# Revit family: Rheem AmbiPower 280e
name_source: partatom
category: Plumbing Fixtures
units: mm (PartAtom-declared; Revit-internal decimal feet)

## family parameters
Always vertical = Yes
Cut with Voids When Loaded = No
Enable Cutting in Views = No
Maintain Annotation Orientation = No
OmniClass Number = 23.45.00.00
OmniClass Title = Sanitary, Laundry, and Cleaning Equipment
Part Type = Normal
Room Calculation Point = No
Round Connector Dimension = Use Diameter
Shared = No
Work Plane-Based = No

## types (1)
- Rheem AmbiPower 280e
    Boost Capacity = 280.0 L
    Coefficient of Performance @19°C = 5.2
    Default Elevation = 0 mm  [stored 0 ft]
    Description = AmbiPower 280e Heat Pump Water Heater
    Electric heating unit rating @ 240 V = 2400 W
    Heater weight - cartoned = 135.00 kg
    Heater weight - full = 402.00 kg
    IP Rating = IP24
    Manufacturer = Rheem
    Maximum rated power input @ 240 V = 3100 W
    Maximun Refrigerant charge = 340gms
    Model = AMBIPOWER A551E280R5
    Operating range = -6° to +43°
    People per household = up to 6
    Rated Heat Pump power input = 690 W
    Recommended electrical circuit = 15 A
    Refrigerant = R290
    Storage Capacity = 236.0 L
    Tank depth = 725 mm  [stored 2.37861 ft]
    Tank height = 1832 mm
    Tank width = 696 mm  [stored 2.28346 ft]
    Type Comments = 208E Heat Pump Water Heater
    URL = https://rheem.co.nz

note: [stored X ft] marks values corroborated as IEEE doubles in the binary element streams (Revit-internal decimal feet)

## geometry (parser evidence)
native form markers: Sweep x3
no freeform markers — native parametric forms only
